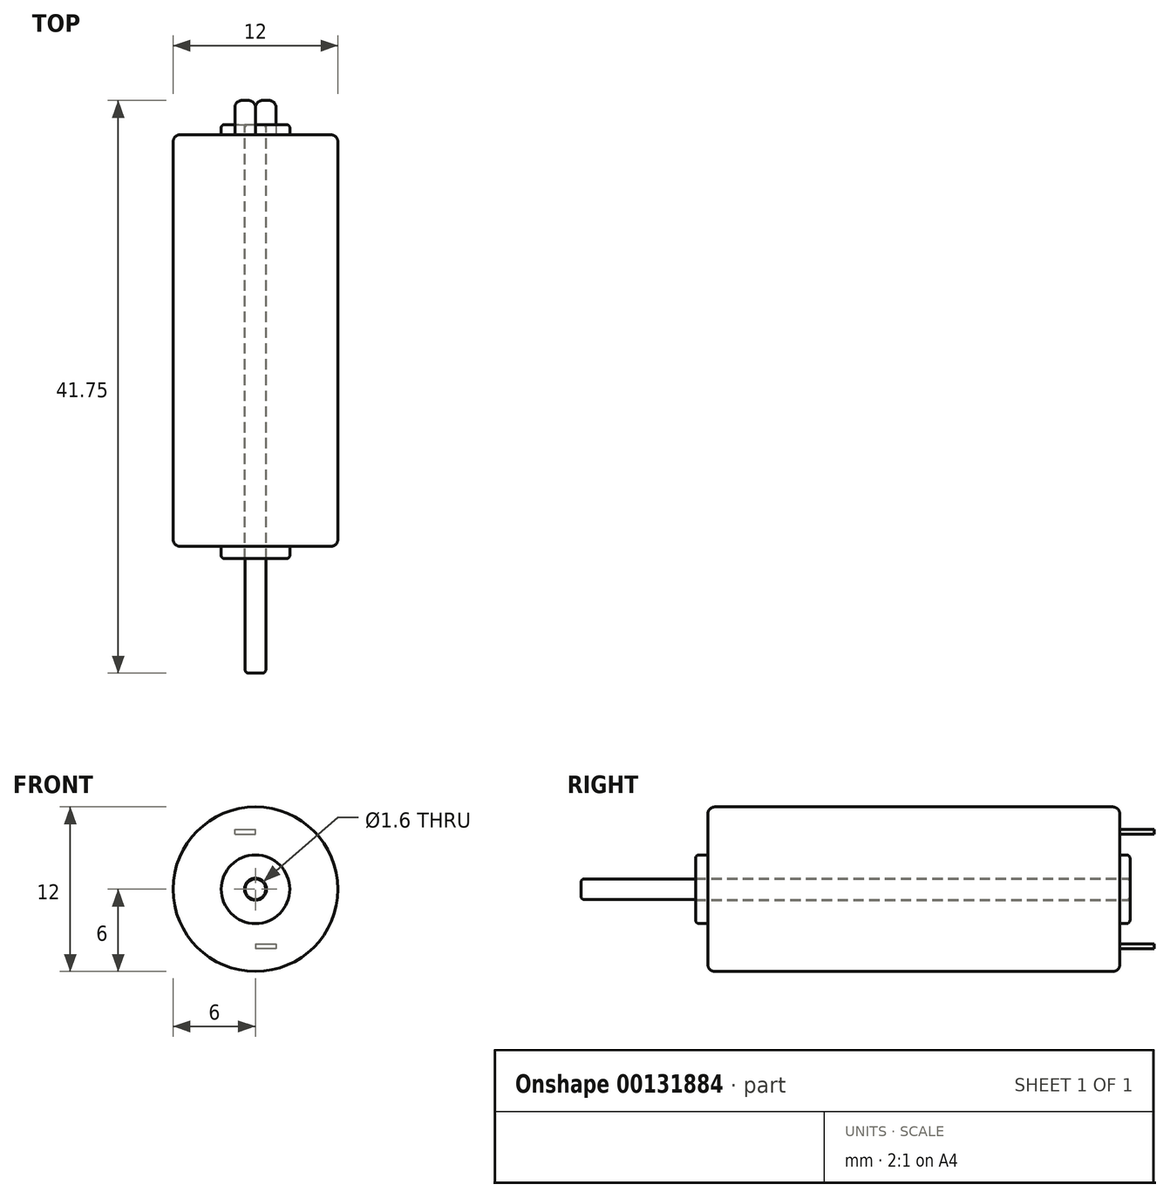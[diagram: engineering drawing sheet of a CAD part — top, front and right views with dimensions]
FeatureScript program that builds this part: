
annotation { "Feature Type Name" : "Feature", "Feature Type Description" : "" }
export const myFeature = defineFeature(function(context is Context, id is Id, definition is map)
    precondition{}
    {
        {
            var Q0;
            Q0=qCreatedBy(makeId("Front.planeOp"),FACE);
            var sketch = newSketch(context, id + "F0", { "sketchPlane" : qUnion([Q0])});
            skCircle(sketch, "E0", {"center": v(0, 0) * mm, "radius": 6 * mm});
            skSolve(sketch);
        }
        {
            var Q0;
            Q0=makeQuery(id+"F0.imprint","IMPRINT",FACE,{"disambiguationData":[TD([[makeQuery(id+"F0.imprint","IMPRINT",EDGE,{"derivedFrom":sQuery(id+"F0.wireOp",EDGE,"E0")}),1.0]])]});
            extrude(context, id + "F1", {"entities" : qUnion([Q0]), "depth" : 28.5 * mm});
        }
        {
            var Q0;
            Q0=makeQuery(id+"F1.opExtrude","CAP_FACE",FACE,{"disambiguationData":[OSD([sQuery(id+"F0.wireOp",EDGE,"E0")])],"isStart":false});
            var sketch = newSketch(context, id + "F2", { "sketchPlane" : qUnion([Q0])});
            skCircle(sketch, "E1", {"center": v(0, 0) * mm, "radius": 2.5 * mm});
            skSolve(sketch);
        }
        {
            var Q0;
            Q0=makeQuery(id+"F2.imprint","IMPRINT",FACE,{"disambiguationData":[TD([[makeQuery(id+"F2.imprint","IMPRINT",EDGE,{"derivedFrom":sQuery(id+"F2.wireOp",EDGE,"E1")}),1.0]])]});
            extrude(context, id + "F3", {"entities" : qUnion([Q0]), "operationType" : NewBodyOperationType.ADD, "depth" : 0.9 * mm});
        }
        {
            var Q0;
            Q0=makeQuery(id+"F1.opExtrude","CAP_FACE",FACE,{"disambiguationData":[OSD([sQuery(id+"F0.wireOp",EDGE,"E0")])],"isStart":true});
            var sketch = newSketch(context, id + "F4", { "sketchPlane" : qUnion([Q0])});
            skCircle(sketch, "E2", {"center": v(0, 0) * mm, "radius": 6 * mm});
            skCircle(sketch, "E3", {"center": v(0, 0) * mm, "radius": 2.5 * mm});
            skSolve(sketch);
        }
        {
            var Q0;
            Q0=makeQuery(id+"F4.imprint","IMPRINT",FACE,{"disambiguationData":[TD([[makeQuery(id+"F4.imprint","IMPRINT",EDGE,{"derivedFrom":sQuery(id+"F4.wireOp",EDGE,"E2")}),-1.0]])]});
            var Q1;
            Q1=makeQuery(id+"F4.imprint","IMPRINT",FACE,{"disambiguationData":[TD([[makeQuery(id+"F4.imprint","IMPRINT",EDGE,{"derivedFrom":sQuery(id+"F4.wireOp",EDGE,"E3")}),1.0]])]});
            extrude(context, id + "F5", {"entities" : qUnion([Q0, Q1]), "operationType" : NewBodyOperationType.ADD, "depth" : 1.5 * mm});
        }
        {
            var Q0;
            Q0=makeQuery(id+"F5.opExtrude","CAP_FACE",FACE,{"disambiguationData":[OSD([sQuery(id+"F4.wireOp",EDGE,"E2")])],"isStart":false});
            var sketch = newSketch(context, id + "F6", { "sketchPlane" : qUnion([Q0])});
            skCircle(sketch, "E4", {"center": v(0, 0) * mm, "radius": 2.5 * mm});
            skSolve(sketch);
        }
        {
            var Q0;
            Q0=makeQuery(id+"F6.imprint","IMPRINT",FACE,{"disambiguationData":[TD([[makeQuery(id+"F6.imprint","IMPRINT",EDGE,{"derivedFrom":sQuery(id+"F6.wireOp",EDGE,"E4")}),1.0]])]});
            extrude(context, id + "F7", {"entities" : qUnion([Q0]), "operationType" : NewBodyOperationType.ADD, "depth" : 0.75 * mm});
        }
        {
            var Q0;
            Q0=qCreatedBy(makeId("Front.planeOp"),FACE);
            var sketch = newSketch(context, id + "F8", { "sketchPlane" : qUnion([Q0])});
            skCircle(sketch, "E5", {"center": v(0, 0) * mm, "radius": 0.8 * mm});
            skSolve(sketch);
        }
        {
            var Q0;
            Q0 = qSketchRegion(id + "F8", true);
            extrude(context, id + "F9", {"entities" : qUnion([Q0]), "operationType" : NewBodyOperationType.REMOVE, "endBound" : BoundingType.SYMMETRIC, "depth" : 60 * mm});
        }
        {
            var Q0;
            Q0=makeQuery(id+"F7.opExtrude","CAP_FACE",FACE,{"disambiguationData":[OSD([sQuery(id+"F6.wireOp",EDGE,"E4")])],"isStart":false});
            var sketch = newSketch(context, id + "F10", { "sketchPlane" : qUnion([Q0])});
            skCircle(sketch, "E6", {"center": v(0, 0) * mm, "radius": 0.75 * mm});
            skSolve(sketch);
        }
        {
            var Q0;
            Q0 = qSketchRegion(id + "F10", true);
            extrude(context, id + "F11", {"entities" : qUnion([Q0]), "oppositeDirection" : true, "depth" : 40 * mm});
        }
        {
            var Q0;
            Q0=makeQuery(id+"F5.opExtrude","CAP_FACE",FACE,{"disambiguationData":[OSD([sQuery(id+"F4.wireOp",EDGE,"E2")])],"isStart":false});
            var sketch = newSketch(context, id + "F12", { "sketchPlane" : qUnion([Q0])});
            skLineSegment(sketch, "E7.bottom", {"start": v(0, -4) * mm, "end": v(-1.5, -4) * mm});
            skLineSegment(sketch, "E7.top", {"start": v(1.5, 4) * mm, "end": v(0, 4) * mm});
            skPoint(sketch, "E7.middle", {"position": v(0, 0) * mm});
            skLineSegment(sketch, "E8.bottom", {"start": v(-1.5, -4) * mm, "end": v(0, -4) * mm});
            skLineSegment(sketch, "E8.top", {"start": v(-1.5, -4.35) * mm, "end": v(0, -4.35) * mm});
            skLineSegment(sketch, "E8.left", {"start": v(-1.5, -4) * mm, "end": v(-1.5, -4.35) * mm});
            skLineSegment(sketch, "E8.right", {"start": v(0, -4) * mm, "end": v(0, -4.35) * mm});
            skLineSegment(sketch, "E9.top", {"start": v(1.5, 4.35) * mm, "end": v(0, 4.35) * mm});
            skLineSegment(sketch, "E9.left", {"start": v(1.5, 4) * mm, "end": v(1.5, 4.35) * mm});
            skLineSegment(sketch, "E9.right", {"start": v(0, 4) * mm, "end": v(0, 4.35) * mm});
            skPoint(sketch, "E10.orphan", {"position": v(-1.5, 4) * mm});
            skPoint(sketch, "E11.orphan", {"position": v(1.5, -4) * mm});
            skSolve(sketch);
        }
        {
            var Q0;
            Q0 = qSketchRegion(id + "F12", true);
            extrude(context, id + "F13", {"entities" : qUnion([Q0]), "operationType" : NewBodyOperationType.ADD, "depth" : 2.5 * mm});
        }
        {
            var Q0;
            Q0=makeQuery(id+"F5.opExtrude","CAP_EDGE",EDGE,{"disambiguationData":[OSD([sQuery(id+"F4.wireOp",EDGE,"E2")])],"isStart":false});
            var Q1;
            Q1=makeQuery(id+"F13.opExtrude","CAP_EDGE",EDGE,{"disambiguationData":[OSD([sQuery(id+"F12.wireOp",EDGE,"E9.left")])],"isStart":false});
            var Q2;
            Q2=makeQuery(id+"F13.opExtrude","CAP_EDGE",EDGE,{"disambiguationData":[OSD([sQuery(id+"F12.wireOp",EDGE,"E9.right")])],"isStart":false});
            var Q3;
            Q3=makeQuery(id+"F13.opExtrude","CAP_EDGE",EDGE,{"disambiguationData":[OSD([sQuery(id+"F12.wireOp",EDGE,"E8.right")])],"isStart":false});
            var Q4;
            Q4=makeQuery(id+"F13.opExtrude","CAP_EDGE",EDGE,{"disambiguationData":[OSD([sQuery(id+"F12.wireOp",EDGE,"E8.left")])],"isStart":false});
            var Q5;
            Q5=makeQuery(id+"F1.opExtrude","CAP_EDGE",EDGE,{"disambiguationData":[OSD([sQuery(id+"F0.wireOp",EDGE,"E0")])],"isStart":false});
            fillet(context, id + "F14", {"entities" : qUnion([Q0, Q1, Q2, Q3, Q4, Q5]), "radius" : .5 * mm, "tangentPropagation" : true, "allowEdgeOverflow" : false});
        }
        {
            var Q0;
            Q0=makeQuery(id+"F3.opExtrude","CAP_EDGE",EDGE,{"disambiguationData":[OSD([sQuery(id+"F2.wireOp",EDGE,"E1")])],"isStart":false});
            var Q1;
            Q1=makeQuery(id+"F7.opExtrude","CAP_EDGE",EDGE,{"disambiguationData":[OSD([sQuery(id+"F6.wireOp",EDGE,"E4")])],"isStart":false});
            var Q2;
            Q2=makeQuery(id+"F11.opExtrude","CAP_FACE",FACE,{"disambiguationData":[OSD([sQuery(id+"F10.wireOp",EDGE,"E6")])],"isStart":true});
            var Q3;
            Q3=makeQuery(id+"F11.opExtrude","CAP_EDGE",EDGE,{"disambiguationData":[OSD([sQuery(id+"F10.wireOp",EDGE,"E6")])],"isStart":false});
            fillet(context, id + "F15", {"entities" : qUnion([Q0, Q1, Q2, Q3]), "radius" : .25 * mm, "tangentPropagation" : true, "allowEdgeOverflow" : false});
        }
    });
